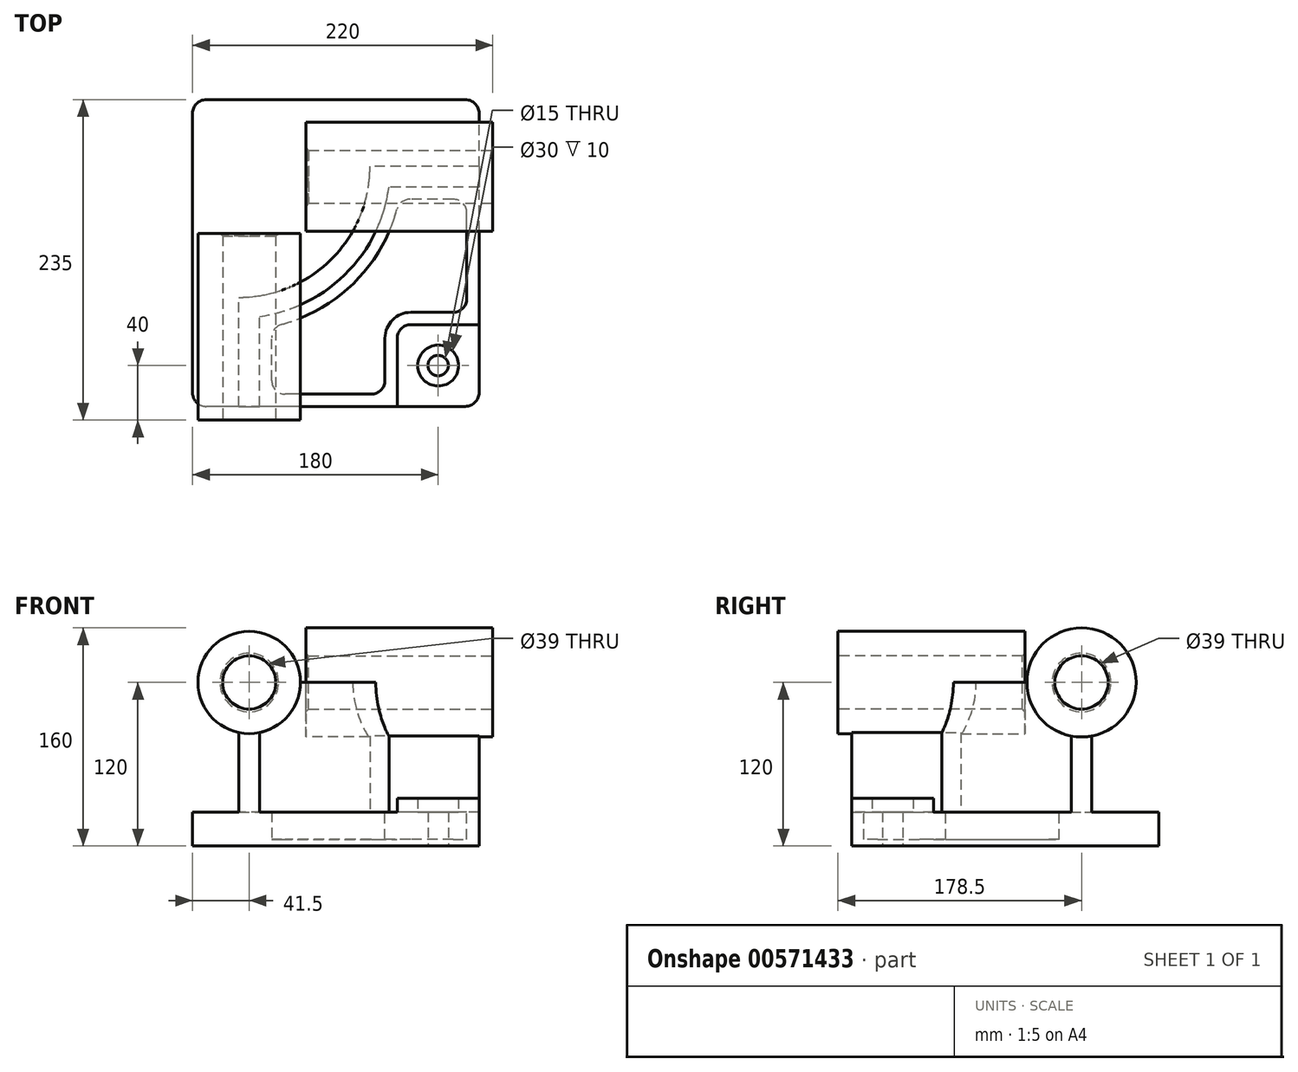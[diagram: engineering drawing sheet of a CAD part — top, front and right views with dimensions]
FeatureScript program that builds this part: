
annotation { "Feature Type Name" : "Feature", "Feature Type Description" : "" }
export const myFeature = defineFeature(function(context is Context, id is Id, definition is map)
    precondition{}
    {
        {
            var Q0;
            Q0=qCreatedBy(makeId("Top.planeOp"),FACE);
            var sketch = newSketch(context, id + "F0", { "sketchPlane" : qUnion([Q0])});
            skLineSegment(sketch, "E0.bottom", {"start": v(105, -112.5) * mm, "end": v(-105, -112.5) * mm});
            skLineSegment(sketch, "E0.top", {"start": v(105, 112.5) * mm, "end": v(-105, 112.5) * mm});
            skLineSegment(sketch, "E0.left", {"start": v(105, -112.5) * mm, "end": v(105, 112.5) * mm});
            skLineSegment(sketch, "E0.right", {"start": v(-105, -112.5) * mm, "end": v(-105, 112.5) * mm});
            skPoint(sketch, "E0.middle", {"position": v(0, 0) * mm});
            skSolve(sketch);
        }
        {
            var Q0;
            Q0=makeQuery(id+"F0.imprint","IMPRINT",FACE,{"disambiguationData":[TD([[makeQuery(id+"F0.imprint","IMPRINT",EDGE,{"derivedFrom":sQuery(id+"F0.wireOp",EDGE,"E0.bottom")}),-1.0]])]});
            extrude(context, id + "F1", {"entities" : qUnion([Q0]), "depth" : 25 * mm, "offsetDistance" : 25.4 * mm});
        }
        {
            var Q0;
            Q0=makeQuery(id+"F1.opExtrude","CAP_FACE",FACE,{"disambiguationData":[OSD([sQuery(id+"F0.wireOp",EDGE,"E0.bottom"),sQuery(id+"F0.wireOp",EDGE,"E0.top"),sQuery(id+"F0.wireOp",EDGE,"E0.left"),sQuery(id+"F0.wireOp",EDGE,"E0.right")])],"isStart":false});
            var sketch = newSketch(context, id + "F2", { "sketchPlane" : qUnion([Q0])});
            skLineSegment(sketch, "E1", {"start": v(-71, -112.5) * mm, "end": v(-71, -32.5) * mm});
            skLineSegment(sketch, "E2", {"start": v(105, 63.5) * mm, "end": v(25, 63.5) * mm});
            skArc(sketch, "E3", {"start": v(-71, -32.5) * mm, "mid": v(-3.12, -4.38) * mm, "end": v(25, 63.5) * mm});
            skLineSegment(sketch, "E4", {"start": v(-71, 63.5) * mm, "end": v(-71, -32.5) * mm, "construction": true});
            skLineSegment(sketch, "E5", {"start": v(-71, 63.5) * mm, "end": v(25, 63.5) * mm, "construction": true});
            skLineSegment(sketch, "E6.0", {"start": v(105, 48.5) * mm, "end": v(38.98, 48.5) * mm});
            skArc(sketch, "E6.1", {"start": v(-56, -46.48) * mm, "mid": v(7.49, -14.99) * mm, "end": v(38.98, 48.5) * mm});
            skLineSegment(sketch, "E6.2", {"start": v(-56, -112.5) * mm, "end": v(-56, -46.48) * mm});
            skLineSegment(sketch, "E7", {"start": v(105, 48.5) * mm, "end": v(105, 63.5) * mm});
            skLineSegment(sketch, "E8", {"start": v(-56, -112.5) * mm, "end": v(-71, -112.5) * mm});
            skSolve(sketch);
        }
        {
            var Q0;
            Q0 = qSketchRegion(id + "F2", true);
            extrude(context, id + "F3", {"entities" : qUnion([Q0]), "operationType" : NewBodyOperationType.ADD, "depth" : 95 * mm, "offsetDistance" : 25.4 * mm});
        }
        {
            var Q0;
            Q0=makeQuery(id+"F3.boolean.opBoolean","MERGE",FACE,{"derivedFrom":[makeQuery(id+"F1.opExtrude","SWEPT_FACE",FACE,{"disambiguationData":[OSD([sQuery(id+"F0.wireOp",EDGE,"E0.bottom")])]}),makeQuery(id+"F3.opExtrude","SWEPT_FACE",FACE,{"disambiguationData":[OSD([sQuery(id+"F2.wireOp",EDGE,"E8")])]})]});
            var sketch = newSketch(context, id + "F4", { "sketchPlane" : qUnion([Q0])});
            skCircle(sketch, "E9", {"center": v(-63.5, 120) * mm, "radius": 37.5 * mm});
            skSolve(sketch);
        }
        {
            var Q0;
            Q0 = qSketchRegion(id + "F4", true);
            extrude(context, id + "F5", {"entities" : qUnion([Q0]), "operationType" : NewBodyOperationType.ADD, "depth" : 10 * mm, "offsetDistance" : 25.4 * mm, "hasSecondDirection" : true, "secondDirectionOppositeDirection" : true, "secondDirectionDepth" : 127 * mm});
        }
        {
            var Q0;
            Q0=makeQuery(id+"F3.boolean.opBoolean","MERGE",FACE,{"derivedFrom":[makeQuery(id+"F1.opExtrude","SWEPT_FACE",FACE,{"disambiguationData":[OSD([sQuery(id+"F0.wireOp",EDGE,"E0.left")])]}),makeQuery(id+"F3.opExtrude","SWEPT_FACE",FACE,{"disambiguationData":[OSD([sQuery(id+"F2.wireOp",EDGE,"E7")])]})]});
            var sketch = newSketch(context, id + "F6", { "sketchPlane" : qUnion([Q0])});
            skCircle(sketch, "E10", {"center": v(56, 120) * mm, "radius": 40 * mm});
            skSolve(sketch);
        }
        {
            var Q0;
            Q0 = qSketchRegion(id + "F6", true);
            extrude(context, id + "F7", {"entities" : qUnion([Q0]), "operationType" : NewBodyOperationType.ADD, "depth" : 10 * mm, "offsetDistance" : 25.4 * mm, "hasSecondDirection" : true, "secondDirectionOppositeDirection" : true, "secondDirectionDepth" : 127 * mm});
        }
        {
            var Q0;
            {var subQ0=sQuery(id+"F0.wireOp",EDGE,"E0.left");var subQ1=sQuery(id+"F0.wireOp",EDGE,"E0.bottom");Q0=makeQuery(id+"F3.boolean.opBoolean","SPLIT",FACE,{"disambiguationData":[TD([makeQuery(id+"F3.opExtrude","SWEPT_FACE",FACE,{"disambiguationData":[OSD([sQuery(id+"F2.wireOp",EDGE,"E6.0")])]})])],"derivedFrom":makeQuery(id+"F1.opExtrude","CAP_FACE",FACE,{"disambiguationData":[OSD([subQ1,sQuery(id+"F0.wireOp",EDGE,"E0.top"),subQ0,sQuery(id+"F0.wireOp",EDGE,"E0.right")])],"isStart":false})});}
            var sketch = newSketch(context, id + "F8", { "sketchPlane" : qUnion([Q0])});
            skLineSegment(sketch, "E11.bottom", {"start": v(105, -112.5) * mm, "end": v(45, -112.5) * mm});
            skLineSegment(sketch, "E11.top", {"start": v(105, -52.5) * mm, "end": v(45, -52.5) * mm});
            skLineSegment(sketch, "E11.left", {"start": v(105, -112.5) * mm, "end": v(105, -52.5) * mm});
            skLineSegment(sketch, "E11.right", {"start": v(45, -112.5) * mm, "end": v(45, -52.5) * mm});
            skSolve(sketch);
        }
        {
            var Q0;
            Q0 = qSketchRegion(id + "F8", true);
            extrude(context, id + "F9", {"entities" : qUnion([Q0]), "operationType" : NewBodyOperationType.ADD, "depth" : 10 * mm, "offsetDistance" : 25.4 * mm});
        }
        {
            var Q0;
            Q0=makeQuery(id+"F9.opExtrude","SWEPT_EDGE",EDGE,{"disambiguationData":[OSD([sQuery(id+"F8.wireOp",EDGE,"E11.top"),sQuery(id+"F8.wireOp",EDGE,"E11.right")])]});
            fillet(context, id + "F10", {"entities" : qUnion([Q0]), "radius" : 10 * mm, "allowEdgeOverflow" : false});
        }
        {
            var Q0;
            {var subQ0=sQuery(id+"F0.wireOp",EDGE,"E0.left");var subQ1=sQuery(id+"F0.wireOp",EDGE,"E0.bottom");Q0=makeQuery(id+"F3.boolean.opBoolean","SPLIT",FACE,{"disambiguationData":[TD([makeQuery(id+"F3.opExtrude","SWEPT_FACE",FACE,{"disambiguationData":[OSD([sQuery(id+"F2.wireOp",EDGE,"E6.0")])]})])],"derivedFrom":makeQuery(id+"F1.opExtrude","CAP_FACE",FACE,{"disambiguationData":[OSD([subQ1,sQuery(id+"F0.wireOp",EDGE,"E0.top"),subQ0,sQuery(id+"F0.wireOp",EDGE,"E0.right")])],"isStart":false})});}
            var sketch = newSketch(context, id + "F11", { "sketchPlane" : qUnion([Q0])});
            skLineSegment(sketch, "E12.0", {"start": v(-47, -103.5) * mm, "end": v(-47, -54.08) * mm});
            skLineSegment(sketch, "E12.1", {"start": v(36, -103.5) * mm, "end": v(-47, -103.5) * mm});
            skArc(sketch, "E12.2", {"start": v(-47, -54.08) * mm, "mid": v(13.85, -21.35) * mm, "end": v(46.58, 39.5) * mm});
            skLineSegment(sketch, "E12.3", {"start": v(36, -103.5) * mm, "end": v(36, -62.5) * mm});
            skLineSegment(sketch, "E12.4", {"start": v(96, 39.5) * mm, "end": v(46.58, 39.5) * mm});
            skLineSegment(sketch, "E12.5", {"start": v(96, -43.5) * mm, "end": v(96, 39.5) * mm});
            skLineSegment(sketch, "E12.6", {"start": v(96, -43.5) * mm, "end": v(55, -43.5) * mm});
            skArc(sketch, "E12.7", {"start": v(55, -43.5) * mm, "mid": v(41.56, -49.06) * mm, "end": v(36, -62.5) * mm});
            skSolve(sketch);
        }
        {
            var Q0;
            Q0=makeQuery(id+"F11.imprint","IMPRINT",FACE,{"disambiguationData":[TD([[makeQuery(id+"F11.imprint","IMPRINT",EDGE,{"derivedFrom":sQuery(id+"F11.wireOp",EDGE,"E12.0")}),-1.0]])]});
            extrude(context, id + "F12", {"entities" : qUnion([Q0]), "operationType" : NewBodyOperationType.REMOVE, "oppositeDirection" : true, "depth" : 20 * mm, "offsetDistance" : 25.4 * mm});
        }
        {
            var Q0;
            Q0=makeQuery(id+"F9.opExtrude","CAP_FACE",FACE,{"disambiguationData":[OSD([sQuery(id+"F8.wireOp",EDGE,"E11.bottom"),sQuery(id+"F8.wireOp",EDGE,"E11.top"),sQuery(id+"F8.wireOp",EDGE,"E11.left"),sQuery(id+"F8.wireOp",EDGE,"E11.right")])],"isStart":false});
            var sketch = newSketch(context, id + "F13", { "sketchPlane" : qUnion([Q0])});
            skCircle(sketch, "E13", {"center": v(75, -82.5) * mm, "radius": 15 * mm});
            skSolve(sketch);
        }
        {
            var Q0;
            Q0=sQuery(id+"F13.wireOp",VERTEX,"E13.center");
            var Q1;
            Q1=makeQuery(id+"F1.opExtrude","SWEPT_BODY",BODY,{"disambiguationData":[OSD([sQuery(id+"F0.wireOp",EDGE,"E0.bottom"),sQuery(id+"F0.wireOp",EDGE,"E0.top"),sQuery(id+"F0.wireOp",EDGE,"E0.left"),sQuery(id+"F0.wireOp",EDGE,"E0.right")])]});
            hole(context, id + "F14", {"style" : HoleStyle.C_BORE, "endStyle" : HoleEndStyle.THROUGH, "holeDiameter" : 15 * mm, "cBoreDiameter" : 30 * mm, "cBoreDepth" : 10 * mm, "isTappedThrough" : true, "tappedDepth" : 12.7 * mm, "tapClearance" : 3, "locations" : qUnion([Q0]), "scope" : qUnion([Q1])});
        }
        {
            var Q0;
            Q0=makeQuery(id+"F12.boolean.opBoolean","COPY",EDGE,{"derivedFrom":makeQuery(id+"F12.opExtrude","SWEPT_EDGE",EDGE,{"disambiguationData":[OSD([sQuery(id+"F11.wireOp",EDGE,"E12.1"),sQuery(id+"F11.wireOp",EDGE,"E12.3")])]})});
            var Q1;
            Q1=makeQuery(id+"F12.boolean.opBoolean","COPY",EDGE,{"derivedFrom":makeQuery(id+"F12.opExtrude","SWEPT_EDGE",EDGE,{"disambiguationData":[OSD([sQuery(id+"F11.wireOp",EDGE,"E12.0"),sQuery(id+"F11.wireOp",EDGE,"E12.1")])]})});
            var Q2;
            Q2=makeQuery(id+"F12.boolean.opBoolean","COPY",EDGE,{"derivedFrom":makeQuery(id+"F12.opExtrude","SWEPT_EDGE",EDGE,{"disambiguationData":[OSD([sQuery(id+"F11.wireOp",EDGE,"E12.0"),sQuery(id+"F11.wireOp",EDGE,"E12.2")])]})});
            var Q3;
            Q3=makeQuery(id+"F12.boolean.opBoolean","COPY",EDGE,{"derivedFrom":makeQuery(id+"F12.opExtrude","SWEPT_EDGE",EDGE,{"disambiguationData":[OSD([sQuery(id+"F11.wireOp",EDGE,"E12.4"),sQuery(id+"F11.wireOp",EDGE,"E12.5")])]})});
            var Q4;
            Q4=makeQuery(id+"F12.boolean.opBoolean","COPY",EDGE,{"derivedFrom":makeQuery(id+"F12.opExtrude","SWEPT_EDGE",EDGE,{"disambiguationData":[OSD([sQuery(id+"F11.wireOp",EDGE,"E12.2"),sQuery(id+"F11.wireOp",EDGE,"E12.4")])]})});
            var Q5;
            Q5=makeQuery(id+"F12.boolean.opBoolean","COPY",EDGE,{"derivedFrom":makeQuery(id+"F12.opExtrude","SWEPT_EDGE",EDGE,{"disambiguationData":[OSD([sQuery(id+"F11.wireOp",EDGE,"E12.5"),sQuery(id+"F11.wireOp",EDGE,"E12.6")])]})});
            fillet(context, id + "F15", {"entities" : qUnion([Q0, Q1, Q2, Q3, Q4, Q5]), "radius" : 10 * mm, "tangentPropagation" : true, "allowEdgeOverflow" : false});
        }
        {
            var Q0;
            Q0=makeQuery(id+"F7.opExtrude","CAP_FACE",FACE,{"disambiguationData":[OSD([sQuery(id+"F6.wireOp",EDGE,"E10")])],"isStart":false});
            var sketch = newSketch(context, id + "F16", { "sketchPlane" : qUnion([Q0])});
            skCircle(sketch, "E14", {"center": v(56, 120) * mm, "radius": 19.5 * mm});
            skSolve(sketch);
        }
        {
            var Q0;
            Q0 = qSketchRegion(id + "F16", true);
            extrude(context, id + "F17", {"entities" : qUnion([Q0]), "operationType" : NewBodyOperationType.REMOVE, "endBound" : BoundingType.THROUGH_ALL, "oppositeDirection" : true, "depth" : 25.4 * mm, "offsetDistance" : 25.4 * mm});
        }
        {
            var Q0;
            Q0=makeQuery(id+"F5.opExtrude","CAP_FACE",FACE,{"disambiguationData":[OSD([sQuery(id+"F4.wireOp",EDGE,"E9")])],"isStart":false});
            var sketch = newSketch(context, id + "F18", { "sketchPlane" : qUnion([Q0])});
            skCircle(sketch, "E15", {"center": v(-63.5, 120) * mm, "radius": 19.5 * mm});
            skSolve(sketch);
        }
        {
            var Q0;
            Q0 = qSketchRegion(id + "F18", true);
            extrude(context, id + "F19", {"entities" : qUnion([Q0]), "operationType" : NewBodyOperationType.REMOVE, "endBound" : BoundingType.THROUGH_ALL, "oppositeDirection" : true, "depth" : 25.4 * mm, "offsetDistance" : 25.4 * mm});
        }
        {
            var Q0;
            Q0=makeQuery(id+"F17.boolean.opBoolean","COPY",EDGE,{"derivedFrom":makeQuery(id+"F17.opExtrude","CAP_EDGE",EDGE,{"disambiguationData":[OSD([sQuery(id+"F16.wireOp",EDGE,"E14")])],"isStart":true})});
            var Q1;
            Q1=makeQuery(id+"F19.boolean.opBoolean","COPY",EDGE,{"derivedFrom":makeQuery(id+"F19.opExtrude","CAP_EDGE",EDGE,{"disambiguationData":[OSD([sQuery(id+"F18.wireOp",EDGE,"E15")])],"isStart":true})});
            var Q2;
            Q2=makeQuery(id+"F17.boolean.opBoolean","INTERSECT",EDGE,{"derivedFrom":[makeQuery(id+"F7.opExtrude","CAP_FACE",FACE,{"disambiguationData":[OSD([sQuery(id+"F6.wireOp",EDGE,"E10")])],"isStart":true}),makeQuery(id+"F17.opExtrude","SWEPT_FACE",FACE,{"disambiguationData":[OSD([sQuery(id+"F16.wireOp",EDGE,"E14")])]})]});
            var Q3;
            Q3=makeQuery(id+"F19.boolean.opBoolean","INTERSECT",EDGE,{"derivedFrom":[makeQuery(id+"F5.opExtrude","CAP_FACE",FACE,{"disambiguationData":[OSD([sQuery(id+"F4.wireOp",EDGE,"E9")])],"isStart":true}),makeQuery(id+"F19.opExtrude","SWEPT_FACE",FACE,{"disambiguationData":[OSD([sQuery(id+"F18.wireOp",EDGE,"E15")])]})]});
            chamfer(context, id + "F20", {"entities" : qUnion([Q0, Q1, Q2, Q3]), "width" : 2 * mm, "tangentPropagation" : true});
        }
        {
            var Q0;
            Q0=makeQuery(id+"F9.boolean.opBoolean","MERGE",EDGE,{"derivedFrom":[makeQuery(id+"F1.opExtrude","SWEPT_EDGE",EDGE,{"disambiguationData":[OSD([sQuery(id+"F0.wireOp",EDGE,"E0.bottom"),sQuery(id+"F0.wireOp",EDGE,"E0.left")])]}),makeQuery(id+"F9.opExtrude","SWEPT_EDGE",EDGE,{"disambiguationData":[OSD([sQuery(id+"F8.wireOp",EDGE,"E11.bottom"),sQuery(id+"F8.wireOp",EDGE,"E11.left")])]})]});
            var Q1;
            Q1=makeQuery(id+"F1.opExtrude","SWEPT_EDGE",EDGE,{"disambiguationData":[OSD([sQuery(id+"F0.wireOp",EDGE,"E0.top"),sQuery(id+"F0.wireOp",EDGE,"E0.left")])]});
            var Q2;
            Q2=makeQuery(id+"F1.opExtrude","SWEPT_EDGE",EDGE,{"disambiguationData":[OSD([sQuery(id+"F0.wireOp",EDGE,"E0.bottom"),sQuery(id+"F0.wireOp",EDGE,"E0.right")])]});
            var Q3;
            Q3=makeQuery(id+"F1.opExtrude","SWEPT_EDGE",EDGE,{"disambiguationData":[OSD([sQuery(id+"F0.wireOp",EDGE,"E0.top"),sQuery(id+"F0.wireOp",EDGE,"E0.right")])]});
            fillet(context, id + "F21", {"entities" : qUnion([Q0, Q1, Q2, Q3]), "radius" : 10 * mm, "tangentPropagation" : true, "allowEdgeOverflow" : false});
        }
    });
